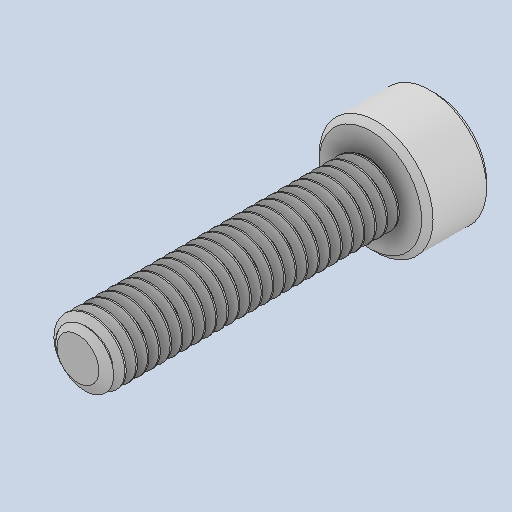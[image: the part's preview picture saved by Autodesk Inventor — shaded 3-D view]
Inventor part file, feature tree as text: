
AUTODESK INVENTOR PART (.ipt)
format: ipt  version: 2023 (Build 270158000, 158)  size: 863,232 bytes
history: native  units: in
note: dims shown in document units (in); Inventor stores cm internally (conversion verified against a paired STEP export)
features: chamfer x1
ambient origin geometry x8: Origin, YZ Plane, XZ Plane, XY Plane, X Axis, Y Axis, Z Axis, Center Point
bodies: Solid1 (feature_tree)
feature tree (1):
  chamfer  "Chamfer1"  [1 undecoded]
note: 1 required parameter value undecoded (feature->parameter linkage not recoverable at this tier; creation-order binding heuristic only, values carry confidence <= 0.55)
